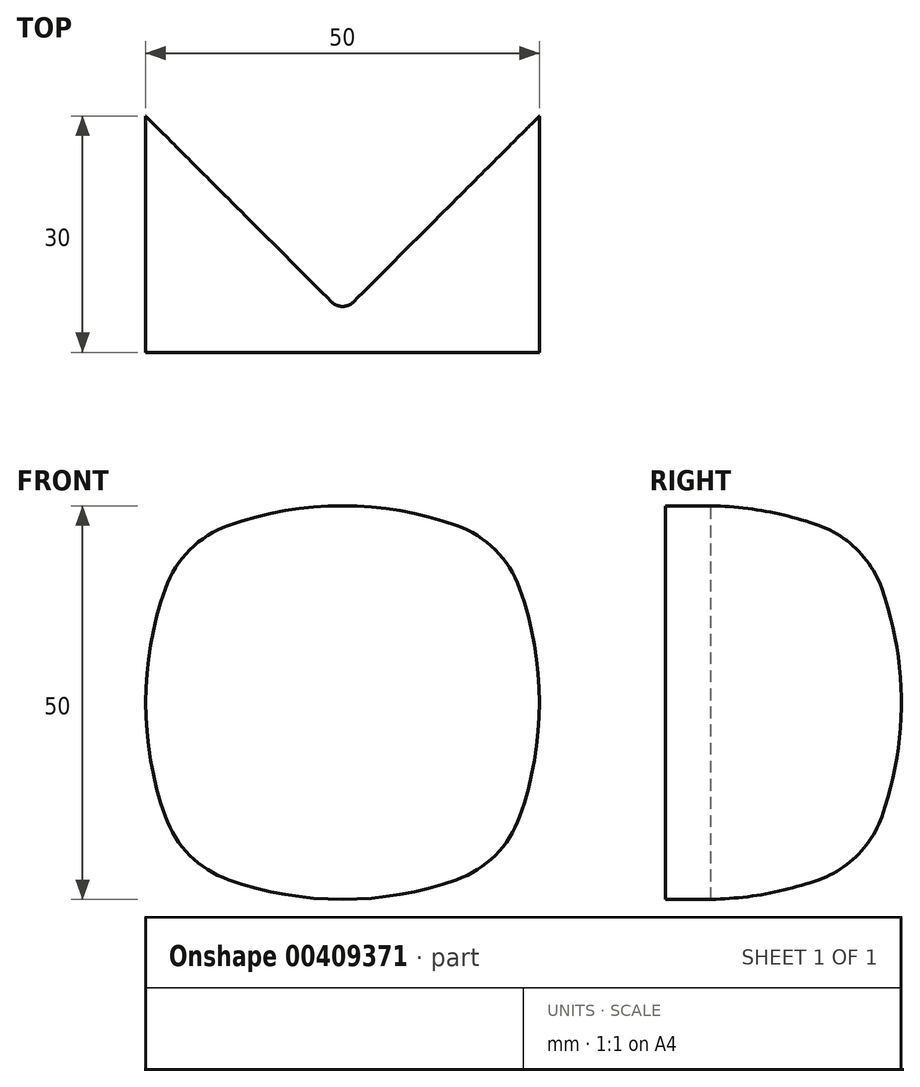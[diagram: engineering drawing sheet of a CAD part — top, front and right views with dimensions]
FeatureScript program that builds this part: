
annotation { "Feature Type Name" : "Feature", "Feature Type Description" : "" }
export const myFeature = defineFeature(function(context is Context, id is Id, definition is map)
    precondition{}
    {
        {
            var Q0;
            Q0=qCreatedBy(makeId("Front.planeOp"),FACE);
            var sketch = newSketch(context, id + "F0", { "sketchPlane" : qUnion([Q0])});
            skLineSegment(sketch, "E0.bottom", {"start": v(22.5, -22.5) * mm, "end": v(-22.5, -22.5) * mm, "construction": true});
            skLineSegment(sketch, "E0.top", {"start": v(22.5, 22.5) * mm, "end": v(-22.5, 22.5) * mm, "construction": true});
            skLineSegment(sketch, "E0.left", {"start": v(22.5, -22.5) * mm, "end": v(22.5, 22.5) * mm, "construction": true});
            skLineSegment(sketch, "E0.right", {"start": v(-22.5, -22.5) * mm, "end": v(-22.5, 22.5) * mm, "construction": true});
            skPoint(sketch, "E0.middle", {"position": v(0, 0) * mm});
            skPoint(sketch, "E1", {"position": v(-22.5, -14.5) * mm});
            skPoint(sketch, "E2", {"position": v(-14.5, -22.5) * mm});
            skPoint(sketch, "E3", {"position": v(-22.5, 14.5) * mm});
            skPoint(sketch, "E4", {"position": v(-14.5, 22.5) * mm});
            skPoint(sketch, "E5", {"position": v(0, 25) * mm});
            skPoint(sketch, "E5.positionSnap0", {"position": v(0, 22.5) * mm});
            skPoint(sketch, "E6", {"position": v(0, -25) * mm});
            skLineSegment(sketch, "E7", {"start": v(0, 25) * mm, "end": v(22.38, 25) * mm, "construction": true});
            skArc(sketch, "E8", {"start": v(0, 25) * mm, "mid": v(-7.36, 24.37) * mm, "end": v(-14.5, 22.5) * mm});
            skLineSegment(sketch, "E9", {"start": v(0, -25) * mm, "end": v(22.5, -25) * mm, "construction": true});
            skArc(sketch, "E10", {"start": v(0, -25) * mm, "mid": v(-7.36, -24.37) * mm, "end": v(-14.5, -22.5) * mm});
            skPoint(sketch, "E11", {"position": v(-25, 0) * mm});
            skLineSegment(sketch, "E12", {"start": v(-25, 0) * mm, "end": v(-25, -6.96) * mm, "construction": true});
            skLineSegment(sketch, "E13", {"start": v(-25, 0) * mm, "end": v(-25, 5.2) * mm, "construction": true});
            skArc(sketch, "E14", {"start": v(-25, 0) * mm, "mid": v(-24.37, -7.36) * mm, "end": v(-22.5, -14.5) * mm});
            skArc(sketch, "E15", {"start": v(-25, 0) * mm, "mid": v(-24.37, 7.36) * mm, "end": v(-22.5, 14.5) * mm});
            skArc(sketch, "E16", {"start": v(-22.5, -14.5) * mm, "mid": v(-19.4, -19.4) * mm, "end": v(-14.5, -22.5) * mm});
            skArc(sketch, "E17", {"start": v(-22.5, 14.5) * mm, "mid": v(-19.4, 19.4) * mm, "end": v(-14.5, 22.5) * mm});
            skArc(sketch, "E18.MirrorCS", {"start": v(0, 25) * mm, "mid": v(7.36, 24.37) * mm, "end": v(14.5, 22.5) * mm});
            skArc(sketch, "E19.MirrorCS", {"start": v(22.5, 14.5) * mm, "mid": v(19.4, 19.4) * mm, "end": v(14.5, 22.5) * mm});
            skArc(sketch, "E20.MirrorCS", {"start": v(25, 0) * mm, "mid": v(24.37, 7.36) * mm, "end": v(22.5, 14.5) * mm});
            skArc(sketch, "E21.MirrorCS", {"start": v(25, 0) * mm, "mid": v(24.37, -7.36) * mm, "end": v(22.5, -14.5) * mm});
            skArc(sketch, "E22.MirrorCS", {"start": v(22.5, -14.5) * mm, "mid": v(19.4, -19.4) * mm, "end": v(14.5, -22.5) * mm});
            skArc(sketch, "E23.MirrorCS", {"start": v(0, -25) * mm, "mid": v(7.36, -24.37) * mm, "end": v(14.5, -22.5) * mm});
            skSolve(sketch);
        }
        {
            var Q0;
            Q0 = qSketchRegion(id + "F0", true);
            extrude(context, id + "F1", {"entities" : qUnion([Q0]), "oppositeDirection" : true, "depth" : 50 * mm, "hasSecondDirection" : true, "secondDirectionOppositeDirection" : false, "secondDirectionDepth" : 5 * mm});
        }
        {
            var Q0;
            Q0=qCreatedBy(makeId("Top.planeOp"),FACE);
            var sketch = newSketch(context, id + "F2", { "sketchPlane" : qUnion([Q0])});
            skLineSegment(sketch, "E24", {"start": v(0, 0) * mm, "end": v(25, 25) * mm});
            skLineSegment(sketch, "E25", {"start": v(25, 25) * mm, "end": v(25, 50) * mm});
            skLineSegment(sketch, "E26", {"start": v(25, 50) * mm, "end": v(0, 50) * mm});
            skLineSegment(sketch, "E27.MirrorCS", {"start": v(-25, 50) * mm, "end": v(0, 50) * mm});
            skLineSegment(sketch, "E28.MirrorCS", {"start": v(-25, 25) * mm, "end": v(-25, 50) * mm});
            skLineSegment(sketch, "E29.MirrorCS", {"start": v(0, 0) * mm, "end": v(-25, 25) * mm});
            skSolve(sketch);
        }
        {
            var Q0;
            Q0 = qSketchRegion(id + "F2", true);
            extrude(context, id + "F3", {"entities" : qUnion([Q0]), "operationType" : NewBodyOperationType.REMOVE, "endBound" : BoundingType.THROUGH_ALL, "oppositeDirection" : true, "depth" : 25 * mm, "hasSecondDirection" : true, "secondDirectionBound" : SecondDirectionBoundingType.THROUGH_ALL, "secondDirectionOppositeDirection" : false, "secondDirectionDepth" : 25 * mm});
        }
        {
            var Q0;
            Q0=makeQuery(id+"F3.boolean.opBoolean","COPY",EDGE,{"derivedFrom":makeQuery(id+"F3.opExtrude","SWEPT_EDGE",EDGE,{"disambiguationData":[OSD([sQuery(id+"F2.wireOp",EDGE,"E24"),sQuery(id+"F2.wireOp",EDGE,"E29.MirrorCS")])]})});
            fillet(context, id + "F4", {"entities" : qUnion([Q0]), "radius" : 2 * mm, "tangentPropagation" : true, "allowEdgeOverflow" : false});
        }
    });
